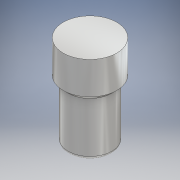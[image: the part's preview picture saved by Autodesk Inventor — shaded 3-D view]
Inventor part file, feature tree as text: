
AUTODESK INVENTOR PART (.ipt)
format: ipt  version: 2018.3 (Build 223284000, 284)  size: 118,784 bytes
history: native  units: mm
features: extrude x2, sketch x2, fillet x1, chamfer x1
ambient origin geometry x8: Origin, YZ Plane, XZ Plane, XY Plane, X Axis, Y Axis, Z Axis, Center Point
bodies: Solid1 (feature_tree)
feature tree (6):
  extrude  "Extrusion1"  Depth=36.0mm TaperAngle=0.0deg
  extrude  "Extrusion2"  Depth=2.0mm TaperAngle=0.0deg
  fillet  "Fillet1"  Radius=2.0mm
  chamfer  "Chamfer1"  Distance=2.0mm Angle=45.0deg
  sketch  "Sketch1"  dims[d0=27.0mm d1=36.0mm d2=0.0mm]
  sketch  "Sketch2"  dims[d3=33.0mm d4=20.0mm d5=0.0mm d6=2.0mm d7=3.0mm d8=2.0mm d9=45.0deg]
